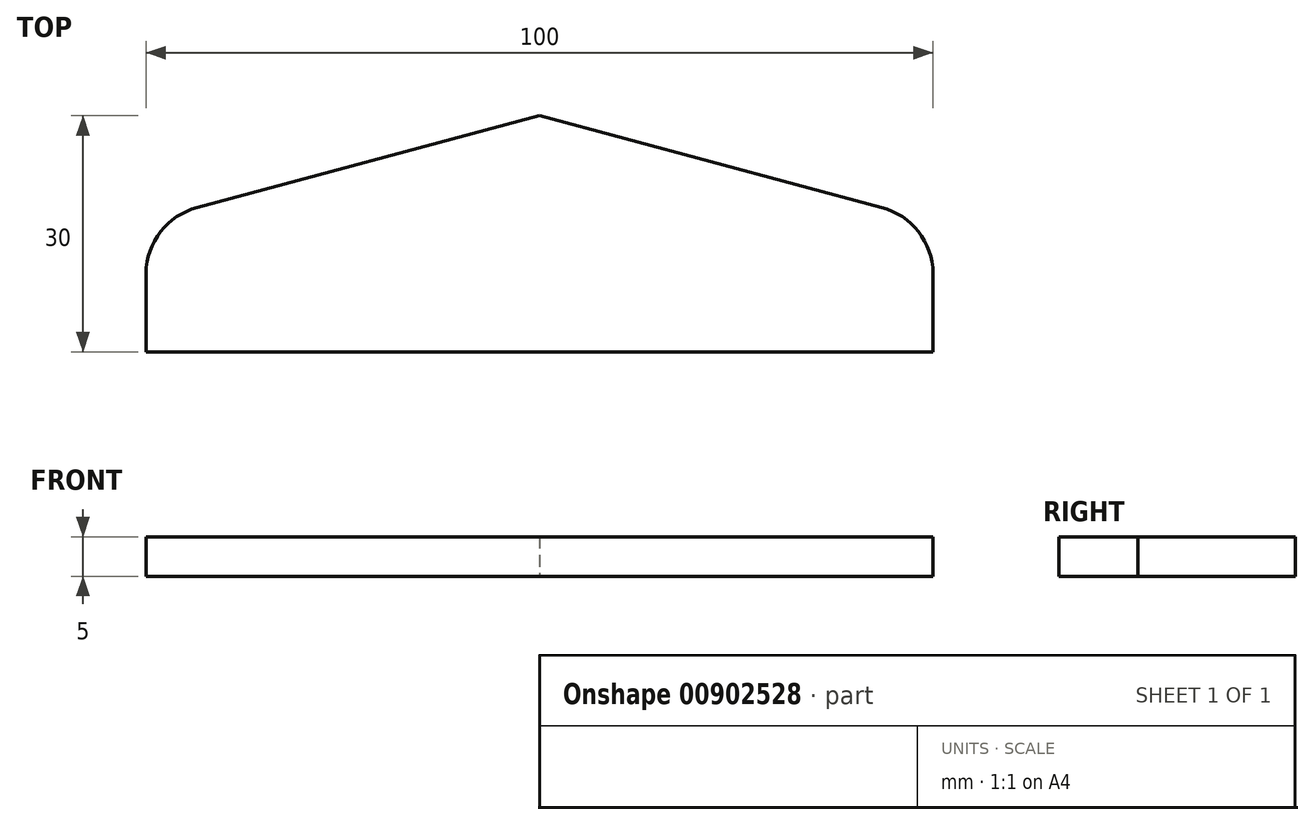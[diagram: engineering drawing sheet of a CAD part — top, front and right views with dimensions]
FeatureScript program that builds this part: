
annotation { "Feature Type Name" : "Feature", "Feature Type Description" : "" }
export const myFeature = defineFeature(function(context is Context, id is Id, definition is map)
    precondition{}
    {
        {
            var Q0;
            Q0=qCreatedBy(makeId("Top.planeOp"),FACE);
            var sketch = newSketch(context, id + "F0", { "sketchPlane" : qUnion([Q0])});
            skLineSegment(sketch, "E0", {"start": v(0, 0) * mm, "end": v(50, 0) * mm});
            skLineSegment(sketch, "E1", {"start": v(50, 0) * mm, "end": v(50, 10) * mm});
            skLineSegment(sketch, "E2", {"start": v(0, 0) * mm, "end": v(0, 30) * mm});
            skLineSegment(sketch, "E3", {"start": v(0, 30) * mm, "end": v(43.46, 18.34) * mm});
            skArc(sketch, "E4", {"start": v(43.46, 18.34) * mm, "mid": v(48.12, 15.26) * mm, "end": v(50, 10) * mm});
            skLineSegment(sketch, "E5.MirrorCS", {"start": v(0, 30) * mm, "end": v(-43.46, 18.34) * mm});
            skLineSegment(sketch, "E6.MirrorCS", {"start": v(0, 0) * mm, "end": v(-50, 0) * mm});
            skLineSegment(sketch, "E7.MirrorCS", {"start": v(-50, 0) * mm, "end": v(-50, 10) * mm});
            skArc(sketch, "E8.MirrorCS", {"start": v(-43.46, 18.34) * mm, "mid": v(-48.12, 15.26) * mm, "end": v(-50, 10) * mm});
            skSolve(sketch);
        }
        {
            var Q0;
            Q0=makeQuery(id+"F0.imprint","IMPRINT",FACE,{"disambiguationData":[TD([[makeQuery(id+"F0.imprint","IMPRINT",EDGE,{"derivedFrom":sQuery(id+"F0.wireOp",EDGE,"E2")}),1.0]])]});
            var Q1;
            Q1=makeQuery(id+"F0.imprint","IMPRINT",FACE,{"disambiguationData":[TD([[makeQuery(id+"F0.imprint","IMPRINT",EDGE,{"derivedFrom":sQuery(id+"F0.wireOp",EDGE,"E0")}),1.0]])]});
            extrude(context, id + "F1", {"entities" : qUnion([Q0, Q1]), "depth" : 5 * mm, "offsetDistance" : 25 * mm});
        }
    });
